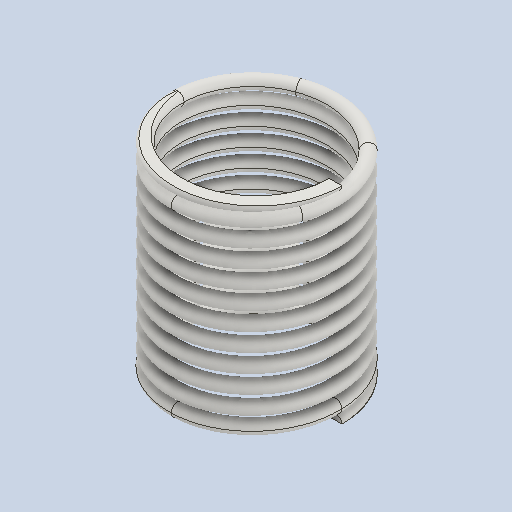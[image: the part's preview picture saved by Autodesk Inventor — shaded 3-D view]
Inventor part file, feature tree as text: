
AUTODESK INVENTOR PART (.ipt)
format: ipt  version: 2025 (Build 290162010, 162A)  size: 1,084,416 bytes
history: native  units: mm
features: other x65, extrude x8, plane x5, helix x3, sketch x3, sweep x2
ambient origin geometry x8: Origin, YZ Plane, XZ Plane, XY Plane, X Axis, Y Axis, Z Axis, Center Point
bodies: Solid1 (feature_tree)
feature tree (86):
  other  "Hauptschraubenpfad(Rechts)"
  other  "Profilarbeitsebene(Rechts)"
  plane  "Arbeitsebene(Rechts) starten"
  plane  "Arbeitsebene(Rechts) beenden"
  other  "Schnittarbeitsebene(Rechts) beenden"
  other  "Schnittarbeitsebene(Rechts) starten"
  other  "Schnittarbeitsebene mit flachen Enden 1(Rechts)"
  other  "Schnittarbeitsebene mit flachen Enden 2(Rechts)"
  sweep  "Main Coil Feature(R)"
  other  "Übergangsschraube 1(Rechts) starten"
  helix  "Coil  Start Transition 2(R)"  [1 undecoded]
  helix  "Coil  Start Transition 3(R)"  [1 undecoded]
  helix  "Coil  Start Transition 4(R)"  [1 undecoded]
  other  "Endenschraube(Rechts) starten"
  extrude  "Schnittelement(Rechts) starten"  Depth=10.0mm
  other  "Übergangsschraube 1(Rechts) beenden"
  other  "Übergangsschraube 2(Rechts) beenden"
  other  "Übergangsschraube 3(Rechts) beenden"
  other  "Übergangsschraube 4(Rechts) beenden"
  other  "Spirale(Rechts) beenden"
  extrude  "Schnittelement(Rechts) beenden"  Depth=10.0mm
  extrude  "Schnittelement mit flachen Enden 1(Rechts)"  Depth=10.0mm
  extrude  "Plain Ends Cut  2(R)"  Depth=10.0mm TaperAngle=0.0deg
  other  "Hauptschraubenpfad(Links)"
  other  "Profilarbeitsebene(Links)"
  plane  "Arbeitsebene(Links) starten"
  plane  "Arbeitsebene(Links) beenden"
  other  "Schnittarbeitsebene(Links) beenden"
  other  "Schnittarbeitsebene(Links) starten"
  other  "Schnittarbeitsebene mit flachen Enden 1(Links)"
  other  "Schnittarbeitsebene mit flachen Enden 2(Links)"
  sweep  "Main Coil Feature(L)"
  other  "Übergangsschraube 1(Links) starten"
  other  "Übergangsschraube 2(Links) starten"
  other  "Übergangsschraube 3(Links) starten"
  other  "Übergangsschraube 4(Links) starten"
  other  "Endenschraube(Links) starten"
  extrude  "Schnittelement(Links) starten"  Depth=10.0mm TaperAngle=0.0deg
  other  "Übergangsschraube 1(Links) beenden"
  other  "Übergangsschraube 2(Links) beenden"
  other  "Übergangsschraube 3(Links) beenden"
  other  "Übergangsschraube 4(Links) beenden"
  other  "Spirale(Links) beenden"
  extrude  "Schnittelement(Links) beenden"  Depth=10.0mm
  extrude  "Cut Plain Ends Cut 1(L)"  TaperAngle=0.0deg  [1 undecoded]
  extrude  "Cut Plain Ends Cut 2(L)"  TaperAngle=0.0deg  [1 undecoded]
  other  "iMate-basierte Arbeitsebene"
  other  "Vorschau Mittelpunkt"
  other  "Vorschau X-Achse"
  other  "Pfadprofilskizze(Rechts)"
  other  "Srf1"
  other  "Spiralenprofilskizze(Rechts)"
  other  "Übergangsschraubenskizze 1(Rechts) starten"
  sketch  "Sketch  Start Transition 2(R)"  dims[d0=0.125mm d2=0.701927mm d3=10.0mm d4=92.5mm]
  sketch  "Sketch  Start Transition 3(R)"  dims[d5=0.0mm d6=90.0deg d7=90.0deg d8=0.0mm d9=0.0mm d12=0.681625mm d13=-0.825556mm d14=0.5mm]
  sketch  "Sketch  Start Transition 4(R)"  dims[d15=0.0mm d16=0.651446mm d17=10.0mm d18=2.5mm d19=0.0mm d20=90.0deg d21=90.0deg d22=0.0mm d23=0.0mm d24=0.600964mm d25=10.0mm d26=2.5mm d27=0.0mm d28=90.0deg d29=90.0deg d30=0.0mm d31=0.0mm d32=0.550482mm d33=10.0mm d34=2.5mm d35=0.0mm d36=90.0deg d37=90.0deg d38=0.0mm d39=0.0mm d40=0.5mm d41=10.0mm d42=2.5mm d43=0.0mm d44=90.0deg d45=90.0deg d46=0.0mm d47=0.0mm d48=0.651446mm d49=10.0mm d50=1.875mm d51=0.0mm d52=90.0deg d53=90.0deg d54=0.0mm d55=0.0mm d56=0.600964mm d57=10.0mm d58=1.875mm d59=0.0mm d60=90.0deg d61=90.0deg d62=0.0mm d63=0.0mm d64=0.550482mm d65=10.0mm d66=1.875mm d67=0.0mm d68=90.0deg d69=90.0deg d70=0.0mm d71=0.0mm d72=0.5mm d73=10.0mm d74=1.875mm d75=0.0mm d76=90.0deg d77=90.0deg d78=0.0mm d79=0.0mm d81=10.0mm d82=5.0mm d83=0.0mm d84=90.0deg d85=90.0deg d86=0.0mm d87=0.0mm d88=0.500334mm d89=10.0mm d90=5.0mm d91=0.0mm d92=90.0deg d93=90.0deg d94=0.0mm d95=0.0mm d96=6.6153mm d97=0.500334mm d98=0.0mm d99=6.6153mm d100=0.500334mm d101=0.0mm d102=0.0mm d103=0.0mm d104=0.0mm d105=0.0mm d106=0.0mm d108=0.0mm d112=0.0mm d113=0.0mm d114=0.0mm d121=0.000334mm d131=0.0mm d132=0.0mm d133=0.0mm d134=0.0mm d135=0.125mm d137=0.701927mm d138=10.0mm d139=92.5mm d140=0.0mm d141=90.0deg d142=90.0deg d143=0.0mm d144=0.0mm d145=0.681625mm d146=-0.825556mm d147=0.000334mm d148=0.000334mm d149=0.5mm d150=0.0mm d151=0.0mm d152=0.651446mm d153=10.0mm d154=2.5mm d155=0.0mm d156=90.0deg d157=90.0deg d158=0.0mm d159=0.0mm d160=0.600964mm d161=10.0mm d162=2.5mm d163=0.0mm d164=90.0deg d165=90.0deg d166=0.0mm d167=0.0mm d168=0.550482mm d169=10.0mm d170=2.5mm d171=0.0mm d172=90.0deg d173=90.0deg d174=0.0mm d175=0.0mm d176=0.5mm d177=10.0mm d178=2.5mm d179=0.0mm d180=90.0deg d181=90.0deg d182=0.0mm d183=0.0mm d184=10.0mm d185=10.0mm d186=10.0mm d187=10.0mm d188=0.500334mm d189=10.0mm d190=5.0mm d191=0.0mm d192=90.0deg d193=90.0deg d194=0.0mm d195=0.0mm d196=10.0mm d197=6.6153mm d198=0.500334mm d199=0.0mm d200=10.0mm d201=0.651446mm d202=10.0mm d203=1.875mm d204=0.0mm d205=90.0deg d206=90.0deg d207=0.0mm d208=0.0mm d209=10.0mm d210=0.600964mm d211=10.0mm d212=1.875mm d213=0.0mm d214=90.0deg d215=90.0deg d216=0.0mm d217=0.0mm d218=0.550482mm d219=10.0mm d220=1.875mm d221=0.0mm d222=90.0deg d223=90.0deg d224=0.0mm d225=0.0mm d226=0.5mm d227=10.0mm d228=1.875mm d229=0.0mm d230=90.0deg d231=90.0deg d232=0.0mm d233=0.0mm d234=10.0mm d235=10.0mm d236=10.0mm d237=0.500334mm d238=10.0mm d239=5.0mm d240=0.0mm d241=90.0deg d242=90.0deg d243=0.0mm d244=0.0mm d245=6.6153mm d246=0.500334mm d247=0.0mm d248=10.0mm d249=10.0mm d254=6.6153mm d255=10.0mm d256=0.0mm d257=20.0mm d258=-0.000334mm d259=6.6153mm d260=10.0mm d261=0.0mm d262=10.0mm d263=6.6153mm d264=10.0mm d265=0.0mm d266=10.0mm d267=0.0mm d270=-0.763056mm d271=0.0mm d272=6.6153mm d273=10.0mm d274=0.0mm d275=20.0mm d276=-94.24778mm d277=6.1153mm d278=6.1153mm d279=0.0mm d280=0.0mm]
  other  "Übergangsschraubenskizze 1(Rechts) beenden"
  other  "Übergangsschraubenskizze 2(Rechts) beenden"
  other  "Übergangsschraubenskizze 3(Rechts) beenden"
  other  "Übergangsschraubenskizze 4(Rechts) beenden"
  other  "Endenskizze(Rechts) starten"
  other  "Spiralenskizze(Rechts) beenden"
  other  "Schnittskizze(Rechts) beenden"
  other  "Schnittskizze (Rechts) starten"
  other  "Pfadprofilskizze(Links)"
  other  "Srf2"
  other  "Spiralenprofilskizze(Links)"
  other  "Übergangsschraubenskizze 1(Links) starten"
  other  "Übergangsschraubenskizze 2(Links) starten"
  other  "Übergangsschraubenskizze 3(Links) starten"
  other  "Übergangsschraubenskizze 4(Links) starten"
  other  "Endenskizze(Links) starten"
  other  "Schnittskizze(Links) starten"
  other  "Übergangsschraubenskizze 1(Links) beenden"
  other  "Übergangsschraubenskizze 2(Links) beenden"
  other  "Übergangsschraubenskizze 3(Links) beenden"
  other  "Übergangsschraubenskizze 4(Links) beenden"
  other  "Spiralenskizze(Links) beenden"
  other  "Schnittskizze(Links) beenden"
  other  "Schnittskizze mit flachen Enden 2(Links)"
  other  "Schnittskizze mit flachen Enden 2(Rechts)"
  other  "Schnittskizze mit flachen Enden 1(Rechts)"
  other  "Schnittskizze mit flachen Enden 1(Links)"
  plane  "Arbeitsebene - Schnitt starten"
  other  "Basiskurve(Rechts)"
  other  "Basiskurve(Links)"
note: 5 required parameter values undecoded (feature->parameter linkage not recoverable at this tier; creation-order binding heuristic only, values carry confidence <= 0.55)
